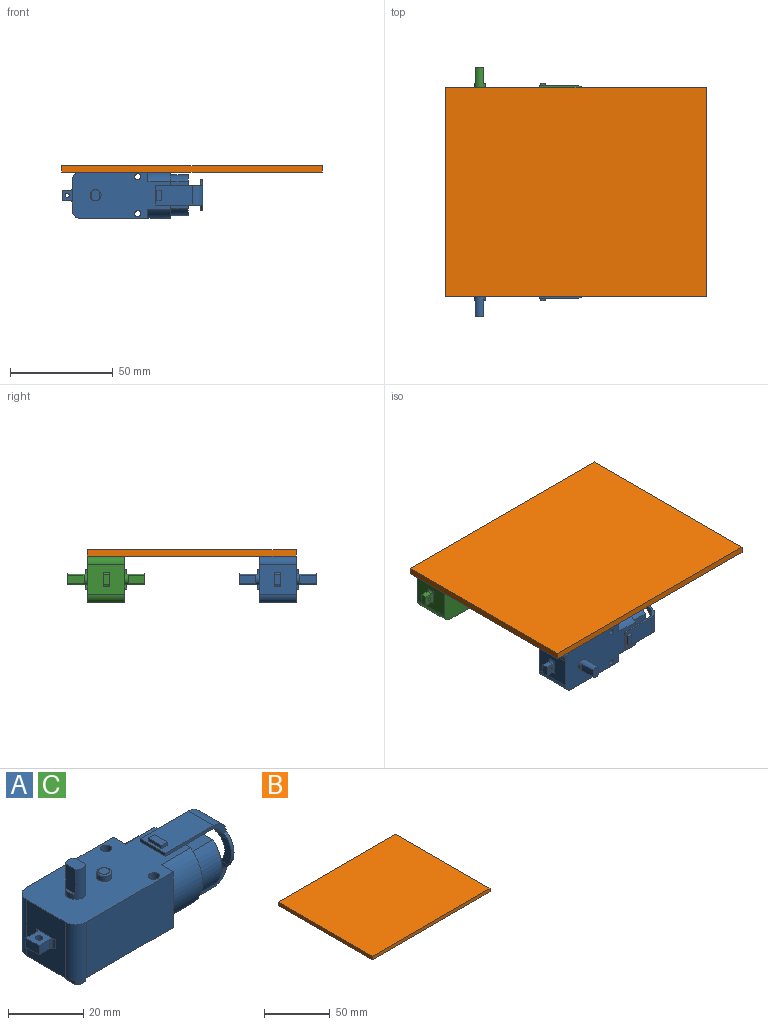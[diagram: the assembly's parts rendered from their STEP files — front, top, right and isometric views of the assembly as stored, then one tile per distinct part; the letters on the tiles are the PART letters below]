
ASSEMBLY  parts=3 mates=2
PART A: 78 faces, bbox 68.5x22.6x37.6 mm
  f0: torus R=1.5mm, axis (0,0,1), area 9mm2, adj f1,f77
  f1: cylinder r=2mm len=4mm, axis (0,0,-1), area 18.8mm2, adj f0,f11
  f2: cylinder r=5mm len=10mm, axis (-1,0,0), area 31.4mm2, adj f8,f47,f60,f62,f74
  f3: cylinder r=1mm len=3mm, axis (0,0,1), area 18.8mm2, adj f23,f25
  f4: cylinder r=1.5mm len=18.2mm, axis (0,0,1), area 171.5mm2, adj f9,f11
  f5: cylinder r=1.5mm len=18.2mm, axis (0,0,1), area 171.5mm2, adj f9,f11
  f6: cylinder r=2.7mm len=9.7mm, axis (0,0,-1), area 94.1mm2, adj f11,f28,f29,f30,f31,f32
  f7: cylinder r=2.7mm len=9.7mm, axis (0,0,1), area 94.1mm2, adj f9,f12,f35,f36,f37,f38
  f8: plane 8.2x4.64mm, normal (-1,0,0), area 22.5mm2, adj f2,f57,f61,f73
  f9: plane 47.9x22.6mm, normal (0,0,-1), area 864.4mm2, adj f4,f5,f7,f14,f15,f16,f17,f19
  f10: plane 9.69x9.5mm, normal (0,0,-1), area 91.4mm2, adj f22,f49,f50,f61,f62,f63
  f11: plane 47.9x22.6mm, normal (0,0,1), area 851.8mm2, adj f1,f4,f5,f6,f13,f16,f17,f18
  f12: plane 5.4x3.7mm, normal (0,0,-1), area 18.3mm2, adj f7,f35,f37
  f13: plane 9.1x4.6mm, normal (1,0,0), area 12.6mm2, adj f11,f16,f20
  f14: plane 9.1x4.6mm, normal (1,0,0), area 12.6mm2, adj f9,f16,f20
  f15: plane 9.1x4.6mm, normal (1,0,0), area 12.6mm2, adj f9,f17,f21
  f16: plane 32.8x18.2mm, normal (0,-1,0), area 597mm2, adj f9,f11,f13,f14,f33
  f17: plane 32.8x18.2mm, normal (0,1,0), area 597mm2, adj f9,f11,f15,f18,f34
  f18: plane 9.1x4.6mm, normal (1,0,0), area 12.6mm2, adj f11,f17,f21
  f19: plane 18.2x14.6mm, normal (-1,0,0), area 244.7mm2, adj f9,f11,f23,f25,f33,f34,f39,f40
  f20: cylinder r=11.3mm len=18.2mm, axis (-1,0,0), area 234.9mm2, adj f9,f11,f13,f14,f22
  f21: cylinder r=11.3mm len=18.2mm, axis (-1,0,0), area 234.9mm2, adj f9,f11,f15,f18,f22
  f22: plane 22.6x18.2mm, normal (1,0,0), area 98.2mm2, adj f9,f10,f11,f20,f21,f41,f42,f43
  f23: plane 7x5mm, normal (0,0,1), area 22.3mm2, adj f3,f19,f24,f26,f27,f39,f40
  f24: plane 4x3mm, normal (0,1,0), area 12mm2, adj f23,f25,f27,f40
  f25: plane 7x5mm, normal (0,0,-1), area 22.3mm2, adj f3,f19,f24,f26,f27,f39,f40
  f26: plane 4x3mm, normal (0,-1,0), area 12mm2, adj f23,f25,f27,f39
  f27: plane 5x3mm, normal (-1,0,0), area 15mm2, adj f23,f24,f25,f26
  f28: plane 5.4x3.7mm, normal (0,0,1), area 18.3mm2, adj f6,f29,f31
  f29: plane 8x3.93mm, normal (1,0,0), area 31.5mm2, adj f6,f28,f30
  f30: plane 3.93x0.85mm, normal (0,0,1), area 2.3mm2, adj f6,f29
  f31: plane 8x3.93mm, normal (-1,0,0), area 31.5mm2, adj f6,f28,f32
  f32: plane 3.93x0.85mm, normal (0,0,1), area 2.3mm2, adj f6,f31
  f33: cylinder r=4mm len=18.2mm, axis (0,0,1), area 114.4mm2, adj f9,f11,f16,f19
  f34: cylinder r=4mm len=18.2mm, axis (0,0,-1), area 114.4mm2, adj f9,f11,f17,f19
  f35: plane 8x3.93mm, normal (1,0,0), area 31.5mm2, adj f7,f12,f36
  f36: plane 3.93x0.85mm, normal (0,0,-1), area 2.3mm2, adj f7,f35
  f37: plane 8x3.93mm, normal (-1,0,0), area 31.5mm2, adj f7,f12,f38
  f38: plane 3.93x0.85mm, normal (0,0,-1), area 2.3mm2, adj f7,f37
  f39: cylinder r=1mm len=3mm, axis (0,0,1), area 4.7mm2, adj f19,f23,f25,f26
  f40: cylinder r=1mm len=3mm, axis (0,0,-1), area 4.7mm2, adj f19,f23,f24,f25
  f41: cylinder r=9.9mm len=14.8mm, axis (-1,0,0), area 143.8mm2, adj f22,f42,f44,f45
  f42: plane 13.15x8.6mm, normal (0,0,1), area 113.1mm2, adj f22,f41,f43,f45
  f43: cylinder r=9.9mm len=14.8mm, axis (-1,0,0), area 143.8mm2, adj f22,f42,f44,f45
  f44: plane 13.15x8.6mm, normal (0,0,-1), area 113.1mm2, adj f22,f41,f43,f45
  f45: plane 19.8x14.8mm, normal (1,0,0), area 262.8mm2, adj f41,f42,f43,f44
  f46: plane 18.19x9.5mm, normal (0,0,1), area 161.3mm2, adj f48,f49,f50,f52,f53,f54,f55,f64
  f47: plane 15x10.2mm, normal (1,0,0), area 61.7mm2, adj f2,f57,f58,f64,f76
  f48: plane 9.5x1mm, normal (-1,0,0), area 9.5mm2, adj f11,f46,f49,f50
  f49: plane 23.14x4.3mm, normal (0,1,0), area 26.3mm2, adj f10,f11,f46,f48,f57,f61,f64
  f50: plane 23.14x4.3mm, normal (0,-1,0), area 26.3mm2, adj f10,f11,f46,f48,f58,f63,f64
  f51: plane 5x2.3mm, normal (0,0,1), area 11.5mm2, adj f52,f53,f54,f55
  f52: plane 5x1mm, normal (-1,0,0), area 5mm2, adj f46,f51,f53,f54
  f53: plane 2.3x1mm, normal (0,-1,0), area 2.3mm2, adj f46,f51,f52,f55
  f54: plane 2.3x1mm, normal (0,1,0), area 2.3mm2, adj f46,f51,f52,f55
  f55: plane 5x1mm, normal (1,0,0), area 5mm2, adj f46,f51,f53,f54
  f56: plane 23.14x4.3mm, normal (0,1,0), area 26.3mm2, adj f9,f57,f65,f66,f67,f73,f76
  f57: cylinder r=7.5mm len=11.61mm, axis (-1,0,0), area 13.9mm2, adj f8,f47,f49,f56,f61,f64,f73,f76
  f58: cylinder r=7.5mm len=11.61mm, axis (-1,0,0), area 13.9mm2, adj f47,f50,f59,f60,f63,f64,f75,f76
  f59: plane 23.14x4.3mm, normal (0,-1,0), area 26.3mm2, adj f9,f58,f65,f66,f67,f75,f76
  f60: plane 8.2x4.64mm, normal (-1,0,0), area 22.5mm2, adj f2,f58,f63,f75
  f61: cylinder r=5mm len=5mm, axis (0,1,0), area 16.2mm2, adj f8,f10,f49,f57,f62
  f62: bspline ~5.72x5mm, area 41.5mm2, adj f2,f10,f61,f63
  f63: cylinder r=5mm len=5mm, axis (0,1,0), area 16.2mm2, adj f10,f50,f58,f60,f62
  f64: cylinder r=5mm len=11mm, axis (0,1,0), area 75.1mm2, adj f46,f47,f49,f50,f57,f58
  f65: plane 9.69x9.5mm, normal (0,0,1), area 91.4mm2, adj f22,f56,f59,f73,f74,f75
  f66: plane 18.19x9.5mm, normal (0,0,-1), area 161.3mm2, adj f56,f59,f67,f69,f70,f71,f72,f76
  f67: plane 9.5x1mm, normal (-1,0,0), area 9.5mm2, adj f9,f56,f59,f66
  f68: plane 5x2.3mm, normal (0,0,-1), area 11.5mm2, adj f69,f70,f71,f72
  f69: plane 5x1mm, normal (-1,0,0), area 5mm2, adj f66,f68,f70,f71
  f70: plane 2.3x1mm, normal (0,1,0), area 2.3mm2, adj f66,f68,f69,f72
  f71: plane 2.3x1mm, normal (0,-1,0), area 2.3mm2, adj f66,f68,f69,f72
  f72: plane 5x1mm, normal (1,0,0), area 5mm2, adj f66,f68,f70,f71
  f73: cylinder r=5mm len=5mm, axis (0,-1,0), area 16.2mm2, adj f8,f56,f57,f65,f74
  f74: bspline ~5.72x5mm, area 41.5mm2, adj f2,f65,f73,f75
  f75: cylinder r=5mm len=5mm, axis (0,-1,0), area 16.2mm2, adj f58,f59,f60,f65,f74
  f76: cylinder r=5mm len=11mm, axis (0,-1,0), area 75.1mm2, adj f47,f56,f57,f58,f59,f66
  f77: plane 3x3mm, normal (0,0,1), area 7.1mm2, adj f0
PART B: 6 faces, bbox 127x101.6x3.2 mm
  f0: plane 101.6x3.18mm, normal (1,0,0), area 322.6mm2, adj f1,f3,f4,f5
  f1: plane 127x3.18mm, normal (0,1,0), area 403.2mm2, adj f0,f2,f4,f5
  f2: plane 101.6x3.18mm, normal (-1,0,0), area 322.6mm2, adj f1,f3,f4,f5
  f3: plane 127x3.18mm, normal (0,-1,0), area 403.2mm2, adj f0,f2,f4,f5
  f4: plane 127x101.6mm, normal (0,0,1), area 12903.2mm2, adj f0,f1,f2,f3
  f5: plane 127x101.6mm, normal (0,0,-1), area 12903.2mm2, adj f0,f1,f2,f3
PART C: same geometry as A
PLACE A rot(axis=(-1,0,0),90deg) t=(-57.89,-32.88,-2)mm
PLACE B t=(0.35,-0.07,-2)mm
PLACE C rot(axis=(1,0,0),90deg) t=(-57.89,32.49,-24.6)mm
MATE parallel C.f17 <-> B.f5  axis (0,0,1) through (-37.49,41.59,-2)mm
MATE parallel A.f16 <-> B.f5  axis (0,0,1) through (-37.49,-41.98,-2)mm
